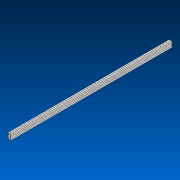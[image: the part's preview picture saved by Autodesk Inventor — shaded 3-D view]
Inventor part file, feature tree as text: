
AUTODESK INVENTOR PART (.ipt)
format: ipt  version: 2022.2 (Build 262287000, 287)  size: 595,456 bytes
history: native  units: in
note: dims shown in document units (in); Inventor stores cm internally (conversion verified against a paired STEP export)
features: other x60, extrude x1, pattern_linear x1, sketch x1
ambient origin geometry x8: Origin, YZ Plane, XZ Plane, XY Plane, X Axis, Y Axis, Z Axis, Center Point
bodies: Solid1 (feature_tree)
feature tree (63):
  extrude  "Extrusion1"  Depth=2.0in
  other  "Work Axis1"
  pattern_linear  "Rectangular Pattern1"  Spacing1=0.0in  [1 undecoded]
  sketch  "Sketch1"  dims[d0=1.0in d1=2.0in d2=0.0in d3=0.0in d4=23.2283in d6=1.0in]
  other  "Work Axis2"
  other  "Work Axis3"
  other  "Work Axis4"
  other  "Work Axis5"
  other  "Work Axis6"
  other  "Work Axis7"
  other  "Work Axis8"
  other  "Work Axis9"
  other  "Work Axis10"
  other  "Work Axis11"
  other  "Work Axis12"
  other  "Work Axis13"
  other  "Work Axis14"
  other  "Work Axis15"
  other  "Work Axis16"
  other  "Work Axis17"
  other  "Work Axis18"
  other  "Work Axis19"
  other  "Work Axis20"
  other  "Work Axis21"
  other  "Work Axis22"
  other  "Work Axis23"
  other  "Work Axis24"
  other  "Work Axis25"
  other  "Work Axis26"
  other  "Work Axis27"
  other  "Work Axis28"
  other  "Work Axis29"
  other  "Work Axis30"
  other  "Work Axis31"
  other  "Work Axis32"
  other  "Work Axis33"
  other  "Work Axis34"
  other  "Work Axis35"
  other  "Work Axis36"
  other  "Work Axis37"
  other  "Work Axis38"
  other  "Work Axis39"
  other  "Work Axis40"
  other  "Work Axis41"
  other  "Work Axis42"
  other  "Work Axis43"
  other  "Work Axis44"
  other  "Work Axis45"
  other  "Work Axis46"
  other  "Work Axis47"
  other  "Work Axis48"
  other  "Work Axis49"
  other  "Work Axis50"
  other  "Work Axis51"
  other  "Work Axis52"
  other  "Work Axis53"
  other  "Work Axis54"
  other  "Work Axis55"
  other  "Work Axis56"
  other  "Work Axis57"
  other  "Work Axis58"
  other  "Work Axis59"
  other  "Cut-Extrude2"
note: 1 required parameter value undecoded (feature->parameter linkage not recoverable at this tier; creation-order binding heuristic only, values carry confidence <= 0.55)
